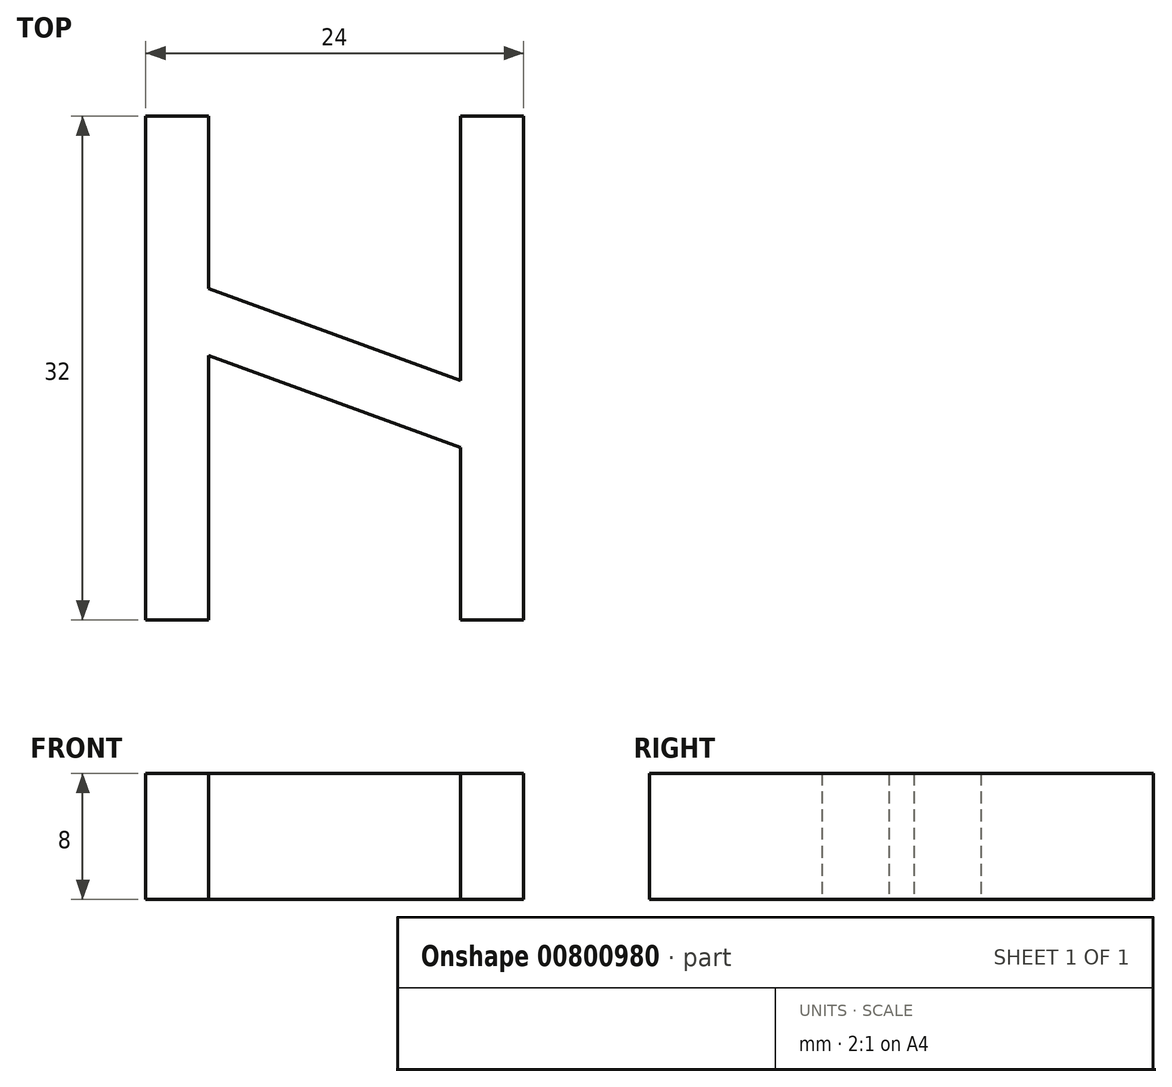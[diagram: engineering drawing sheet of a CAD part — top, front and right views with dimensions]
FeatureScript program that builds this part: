
annotation { "Feature Type Name" : "Feature", "Feature Type Description" : "" }
export const myFeature = defineFeature(function(context is Context, id is Id, definition is map)
    precondition{}
    {
        {
            var Q0;
            Q0=qCreatedBy(makeId("Top.planeOp"),FACE);
            var sketch = newSketch(context, id + "F0", { "sketchPlane" : qUnion([Q0])});
            skLineSegment(sketch, "E0", {"start": v(0, 0) * mm, "end": v(0, -32) * mm});
            skLineSegment(sketch, "E1", {"start": v(0, -32) * mm, "end": v(4, -32) * mm});
            skLineSegment(sketch, "E2", {"start": v(4, -32) * mm, "end": v(4, -15.22) * mm});
            skLineSegment(sketch, "E3", {"start": v(4, -15.22) * mm, "end": v(20, -21.04) * mm});
            skLineSegment(sketch, "E4", {"start": v(20, -21.04) * mm, "end": v(20, -32) * mm});
            skLineSegment(sketch, "E5", {"start": v(20, -32) * mm, "end": v(24, -32) * mm});
            skLineSegment(sketch, "E6", {"start": v(24, -32) * mm, "end": v(24, 0) * mm});
            skLineSegment(sketch, "E7", {"start": v(24, 0) * mm, "end": v(20, 0) * mm});
            skLineSegment(sketch, "E8", {"start": v(20, 0) * mm, "end": v(20, -16.78) * mm});
            skLineSegment(sketch, "E9", {"start": v(20, -16.78) * mm, "end": v(4, -10.96) * mm});
            skLineSegment(sketch, "E10", {"start": v(4, -10.96) * mm, "end": v(4, 0) * mm});
            skLineSegment(sketch, "E11", {"start": v(4, 0) * mm, "end": v(0, 0) * mm});
            skSolve(sketch);
        }
        {
            var Q0;
            Q0=makeQuery(id+"F0.imprint","IMPRINT",FACE,{"disambiguationData":[TD([[makeQuery(id+"F0.imprint","IMPRINT",EDGE,{"derivedFrom":sQuery(id+"F0.wireOp",EDGE,"E0")}),1.0]])]});
            extrude(context, id + "F1", {"entities" : qUnion([Q0]), "depth" : 8 * mm, "offsetDistance" : 25 * mm});
        }
    });
